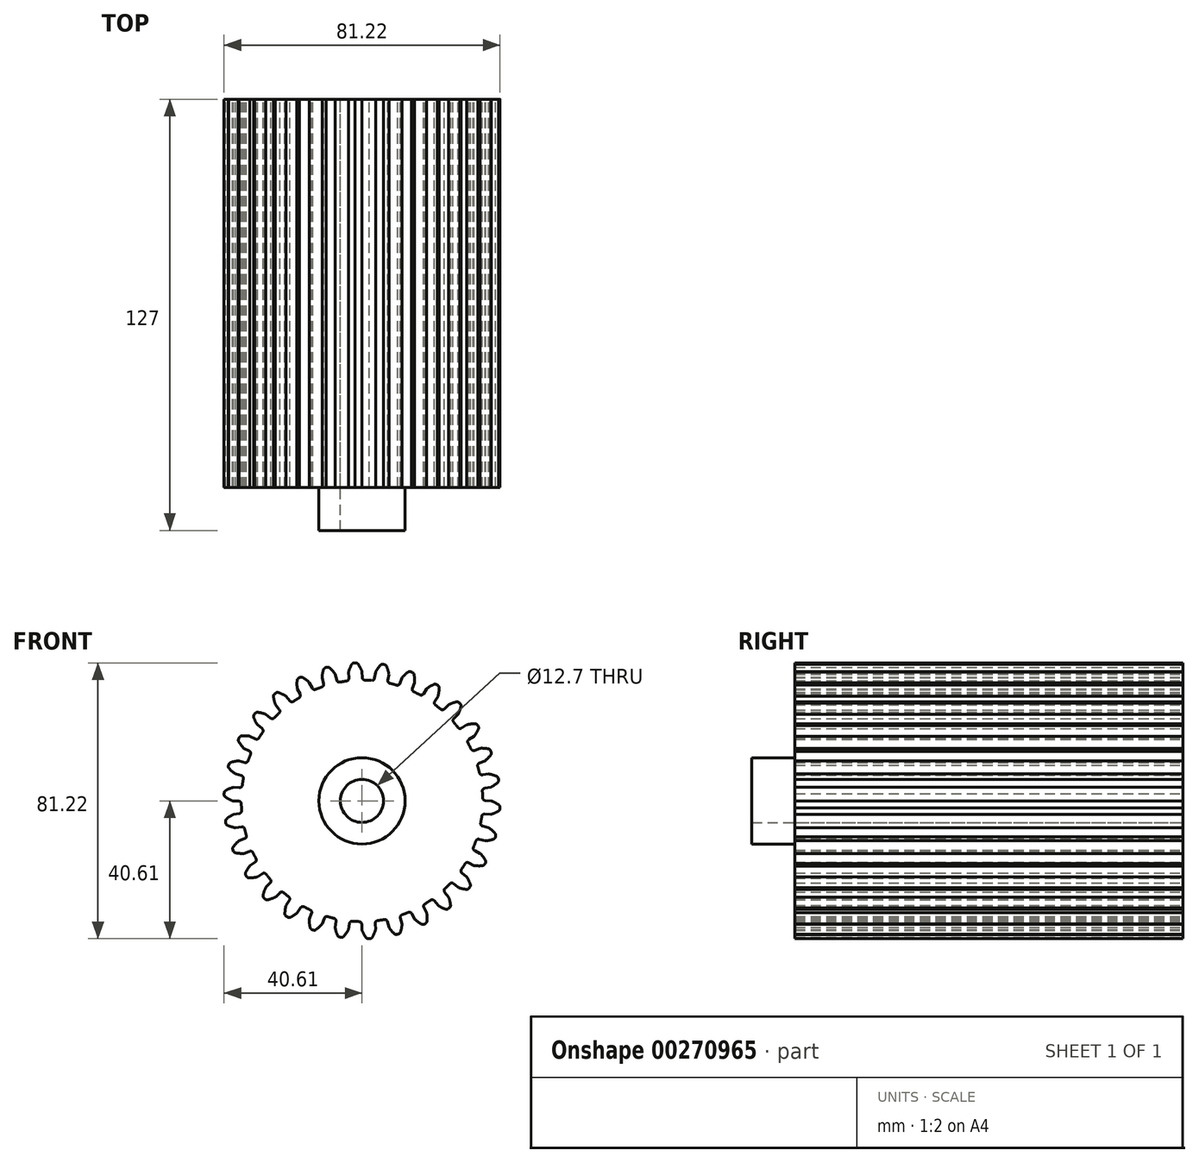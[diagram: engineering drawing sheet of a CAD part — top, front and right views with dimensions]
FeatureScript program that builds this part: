
annotation { "Feature Type Name" : "Feature", "Feature Type Description" : "" }
export const myFeature = defineFeature(function(context is Context, id is Id, definition is map)
    precondition{}
    {
        {
            var Q0;
            Q0=qCreatedBy(makeId("Front.planeOp"),FACE);
            var sketch = newSketch(context, id + "F0", { "sketchPlane" : qUnion([Q0])});
            skArc(sketch, "E0", {"start": v(-4.57, 35.26) * mm, "mid": v(-5.56, 35.12) * mm, "end": v(-6.55, 34.95) * mm});
            skArc(sketch, "E1.trimOffspring", {"start": v(0, 38.1) * mm, "mid": v(-0.52, 39.23) * mm, "end": v(-1.2, 40.3) * mm});
            skLineSegment(sketch, "E2", {"start": v(0, 38.1) * mm, "end": v(0.1, 36.3) * mm});
            skLineSegment(sketch, "E3", {"start": v(-1.83, 40.61) * mm, "end": v(-2.13, 40.61) * mm});
            skLineSegment(sketch, "E4.MirrorCS", {"start": v(-2.43, 40.58) * mm, "end": v(-2.13, 40.61) * mm});
            skArc(sketch, "E5.MirrorCS", {"start": v(-3.98, 37.9) * mm, "mid": v(-3.58, 39.07) * mm, "end": v(-3.03, 40.2) * mm});
            skLineSegment(sketch, "E6.MirrorCS", {"start": v(-3.98, 37.9) * mm, "end": v(-3.89, 36.09) * mm});
            skPoint(sketch, "E7.orphan", {"position": v(-3.43, 27.29) * mm});
            skPoint(sketch, "E8.orphan", {"position": v(0.56, 27.5) * mm});
            skPoint(sketch, "E9.visualSharp", {"position": v(-3.85, 35.35) * mm});
            skArc(sketch, "E9.filletArc", {"start": v(-4.57, 35.26) * mm, "mid": v(-4.07, 35.54) * mm, "end": v(-3.89, 36.09) * mm});
            skPoint(sketch, "E10.visualSharp", {"position": v(0.13, 35.56) * mm});
            skArc(sketch, "E10.filletArc", {"start": v(0.1, 36.3) * mm, "mid": v(0.33, 35.77) * mm, "end": v(0.86, 35.55) * mm});
            skPoint(sketch, "E11.visualSharp", {"position": v(-1.44, 40.61) * mm});
            skArc(sketch, "E11.filletArc", {"start": v(-1.2, 40.3) * mm, "mid": v(-1.47, 40.53) * mm, "end": v(-1.83, 40.61) * mm});
            skPoint(sketch, "E12.visualSharp", {"position": v(-2.81, 40.54) * mm});
            skArc(sketch, "E12.filletArc", {"start": v(-2.43, 40.58) * mm, "mid": v(-2.77, 40.46) * mm, "end": v(-3.03, 40.2) * mm});
            skCircle(sketch, "E13", {"center": v(0, 0) * mm, "radius": 6.35 * mm});
            skLineSegment(sketch, "E14.1.0", {"start": v(-7.92, 37.27) * mm, "end": v(-7.45, 35.52) * mm});
            skArc(sketch, "E14.1.1", {"start": v(-7.45, 35.52) * mm, "mid": v(-7.11, 35.06) * mm, "end": v(-6.55, 34.95) * mm});
            skArc(sketch, "E14.1.2", {"start": v(-7.92, 37.27) * mm, "mid": v(-8.67, 38.27) * mm, "end": v(-9.54, 39.16) * mm});
            skArc(sketch, "E14.1.3", {"start": v(-10.81, 39.2) * mm, "mid": v(-11.12, 39) * mm, "end": v(-11.32, 38.69) * mm});
            skLineSegment(sketch, "E14.1.4", {"start": v(-10.81, 39.2) * mm, "end": v(-10.53, 39.28) * mm});
            skLineSegment(sketch, "E14.1.5", {"start": v(-10.23, 39.35) * mm, "end": v(-10.53, 39.28) * mm});
            skArc(sketch, "E14.1.6", {"start": v(-9.54, 39.16) * mm, "mid": v(-9.87, 39.34) * mm, "end": v(-10.23, 39.35) * mm});
            skArc(sketch, "E14.1.7", {"start": v(-11.77, 36.24) * mm, "mid": v(-11.63, 37.48) * mm, "end": v(-11.32, 38.69) * mm});
            skLineSegment(sketch, "E14.1.8", {"start": v(-11.77, 36.24) * mm, "end": v(-11.3, 34.49) * mm});
            skArc(sketch, "E14.1.9", {"start": v(-11.8, 33.54) * mm, "mid": v(-11.37, 33.92) * mm, "end": v(-11.3, 34.49) * mm});
            skLineSegment(sketch, "E14.2.0", {"start": v(-15.5, 34.8) * mm, "end": v(-14.68, 33.2) * mm});
            skArc(sketch, "E14.2.1", {"start": v(-14.68, 33.2) * mm, "mid": v(-14.25, 32.81) * mm, "end": v(-13.67, 32.83) * mm});
            skArc(sketch, "E14.2.2", {"start": v(-15.5, 34.8) * mm, "mid": v(-16.44, 35.63) * mm, "end": v(-17.48, 36.32) * mm});
            skArc(sketch, "E14.2.3", {"start": v(-18.72, 36.09) * mm, "mid": v(-18.99, 35.84) * mm, "end": v(-19.11, 35.49) * mm});
            skLineSegment(sketch, "E14.2.4", {"start": v(-18.72, 36.09) * mm, "end": v(-18.46, 36.24) * mm});
            skLineSegment(sketch, "E14.2.5", {"start": v(-18.2, 36.36) * mm, "end": v(-18.46, 36.24) * mm});
            skArc(sketch, "E14.2.6", {"start": v(-17.48, 36.32) * mm, "mid": v(-17.83, 36.43) * mm, "end": v(-18.2, 36.36) * mm});
            skArc(sketch, "E14.2.7", {"start": v(-19.05, 33) * mm, "mid": v(-19.16, 34.24) * mm, "end": v(-19.11, 35.49) * mm});
            skLineSegment(sketch, "E14.2.8", {"start": v(-19.05, 33) * mm, "end": v(-18.23, 31.39) * mm});
            skArc(sketch, "E14.2.9", {"start": v(-18.52, 30.36) * mm, "mid": v(-18.17, 30.81) * mm, "end": v(-18.23, 31.39) * mm});
            skLineSegment(sketch, "E14.3.0", {"start": v(-22.4, 30.82) * mm, "end": v(-21.26, 29.42) * mm});
            skArc(sketch, "E14.3.1", {"start": v(-21.26, 29.42) * mm, "mid": v(-20.76, 29.14) * mm, "end": v(-20.2, 29.27) * mm});
            skArc(sketch, "E14.3.2", {"start": v(-22.4, 30.82) * mm, "mid": v(-23.49, 31.43) * mm, "end": v(-24.65, 31.9) * mm});
            skArc(sketch, "E14.3.3", {"start": v(-25.82, 31.4) * mm, "mid": v(-26.03, 31.1) * mm, "end": v(-26.07, 30.74) * mm});
            skLineSegment(sketch, "E14.3.4", {"start": v(-25.82, 31.4) * mm, "end": v(-25.6, 31.6) * mm});
            skLineSegment(sketch, "E14.3.5", {"start": v(-25.35, 31.78) * mm, "end": v(-25.6, 31.6) * mm});
            skArc(sketch, "E14.3.6", {"start": v(-24.65, 31.9) * mm, "mid": v(-25.01, 31.92) * mm, "end": v(-25.35, 31.78) * mm});
            skArc(sketch, "E14.3.7", {"start": v(-25.5, 28.31) * mm, "mid": v(-25.86, 29.5) * mm, "end": v(-26.07, 30.74) * mm});
            skLineSegment(sketch, "E14.3.8", {"start": v(-25.5, 28.31) * mm, "end": v(-24.36, 26.9) * mm});
            skArc(sketch, "E14.3.9", {"start": v(-24.43, 25.84) * mm, "mid": v(-24.18, 26.36) * mm, "end": v(-24.36, 26.9) * mm});
            skLineSegment(sketch, "E14.4.0", {"start": v(-28.31, 25.5) * mm, "end": v(-26.9, 24.36) * mm});
            skArc(sketch, "E14.4.1", {"start": v(-26.9, 24.36) * mm, "mid": v(-26.36, 24.18) * mm, "end": v(-25.84, 24.43) * mm});
            skArc(sketch, "E14.4.2", {"start": v(-28.31, 25.5) * mm, "mid": v(-29.5, 25.86) * mm, "end": v(-30.74, 26.07) * mm});
            skArc(sketch, "E14.4.3", {"start": v(-31.78, 25.35) * mm, "mid": v(-31.92, 25.01) * mm, "end": v(-31.9, 24.65) * mm});
            skLineSegment(sketch, "E14.4.4", {"start": v(-31.78, 25.35) * mm, "end": v(-31.6, 25.6) * mm});
            skLineSegment(sketch, "E14.4.5", {"start": v(-31.4, 25.82) * mm, "end": v(-31.6, 25.6) * mm});
            skArc(sketch, "E14.4.6", {"start": v(-30.74, 26.07) * mm, "mid": v(-31.1, 26.03) * mm, "end": v(-31.4, 25.82) * mm});
            skArc(sketch, "E14.4.7", {"start": v(-30.82, 22.4) * mm, "mid": v(-31.43, 23.49) * mm, "end": v(-31.9, 24.65) * mm});
            skLineSegment(sketch, "E14.4.8", {"start": v(-30.82, 22.4) * mm, "end": v(-29.42, 21.26) * mm});
            skArc(sketch, "E14.4.9", {"start": v(-29.27, 20.2) * mm, "mid": v(-29.14, 20.76) * mm, "end": v(-29.42, 21.26) * mm});
            skLineSegment(sketch, "E14.5.0", {"start": v(-33, 19.05) * mm, "end": v(-31.39, 18.23) * mm});
            skArc(sketch, "E14.5.1", {"start": v(-31.39, 18.23) * mm, "mid": v(-30.81, 18.17) * mm, "end": v(-30.36, 18.52) * mm});
            skArc(sketch, "E14.5.2", {"start": v(-33, 19.05) * mm, "mid": v(-34.24, 19.16) * mm, "end": v(-35.49, 19.11) * mm});
            skArc(sketch, "E14.5.3", {"start": v(-36.36, 18.2) * mm, "mid": v(-36.43, 17.83) * mm, "end": v(-36.32, 17.48) * mm});
            skLineSegment(sketch, "E14.5.4", {"start": v(-36.36, 18.2) * mm, "end": v(-36.24, 18.46) * mm});
            skLineSegment(sketch, "E14.5.5", {"start": v(-36.09, 18.72) * mm, "end": v(-36.24, 18.46) * mm});
            skArc(sketch, "E14.5.6", {"start": v(-35.49, 19.11) * mm, "mid": v(-35.84, 18.99) * mm, "end": v(-36.09, 18.72) * mm});
            skArc(sketch, "E14.5.7", {"start": v(-34.8, 15.5) * mm, "mid": v(-35.63, 16.44) * mm, "end": v(-36.32, 17.48) * mm});
            skLineSegment(sketch, "E14.5.8", {"start": v(-34.8, 15.5) * mm, "end": v(-33.2, 14.68) * mm});
            skArc(sketch, "E14.5.9", {"start": v(-32.83, 13.67) * mm, "mid": v(-32.81, 14.25) * mm, "end": v(-33.2, 14.68) * mm});
            skLineSegment(sketch, "E14.6.0", {"start": v(-36.24, 11.77) * mm, "end": v(-34.49, 11.3) * mm});
            skArc(sketch, "E14.6.1", {"start": v(-34.49, 11.3) * mm, "mid": v(-33.92, 11.37) * mm, "end": v(-33.54, 11.8) * mm});
            skArc(sketch, "E14.6.2", {"start": v(-36.24, 11.77) * mm, "mid": v(-37.48, 11.63) * mm, "end": v(-38.69, 11.32) * mm});
            skArc(sketch, "E14.6.3", {"start": v(-39.35, 10.23) * mm, "mid": v(-39.34, 9.87) * mm, "end": v(-39.16, 9.54) * mm});
            skLineSegment(sketch, "E14.6.4", {"start": v(-39.35, 10.23) * mm, "end": v(-39.28, 10.53) * mm});
            skLineSegment(sketch, "E14.6.5", {"start": v(-39.2, 10.81) * mm, "end": v(-39.28, 10.53) * mm});
            skArc(sketch, "E14.6.6", {"start": v(-38.69, 11.32) * mm, "mid": v(-39, 11.12) * mm, "end": v(-39.2, 10.81) * mm});
            skArc(sketch, "E14.6.7", {"start": v(-37.27, 7.92) * mm, "mid": v(-38.27, 8.67) * mm, "end": v(-39.16, 9.54) * mm});
            skLineSegment(sketch, "E14.6.8", {"start": v(-37.27, 7.92) * mm, "end": v(-35.52, 7.45) * mm});
            skArc(sketch, "E14.6.9", {"start": v(-34.95, 6.55) * mm, "mid": v(-35.06, 7.11) * mm, "end": v(-35.52, 7.45) * mm});
            skLineSegment(sketch, "E14.7.0", {"start": v(-37.9, 3.98) * mm, "end": v(-36.09, 3.89) * mm});
            skArc(sketch, "E14.7.1", {"start": v(-36.09, 3.89) * mm, "mid": v(-35.54, 4.07) * mm, "end": v(-35.26, 4.57) * mm});
            skArc(sketch, "E14.7.2", {"start": v(-37.9, 3.98) * mm, "mid": v(-39.07, 3.58) * mm, "end": v(-40.2, 3.03) * mm});
            skArc(sketch, "E14.7.3", {"start": v(-40.61, 1.83) * mm, "mid": v(-40.53, 1.47) * mm, "end": v(-40.3, 1.2) * mm});
            skLineSegment(sketch, "E14.7.4", {"start": v(-40.61, 1.83) * mm, "end": v(-40.61, 2.13) * mm});
            skLineSegment(sketch, "E14.7.5", {"start": v(-40.58, 2.43) * mm, "end": v(-40.61, 2.13) * mm});
            skArc(sketch, "E14.7.6", {"start": v(-40.2, 3.03) * mm, "mid": v(-40.46, 2.77) * mm, "end": v(-40.58, 2.43) * mm});
            skArc(sketch, "E14.7.7", {"start": v(-38.1, 0) * mm, "mid": v(-39.23, 0.52) * mm, "end": v(-40.3, 1.2) * mm});
            skLineSegment(sketch, "E14.7.8", {"start": v(-38.1, 0) * mm, "end": v(-36.3, -0.1) * mm});
            skArc(sketch, "E14.7.9", {"start": v(-35.55, -0.86) * mm, "mid": v(-35.77, -0.33) * mm, "end": v(-36.3, -0.1) * mm});
            skLineSegment(sketch, "E14.8.0", {"start": v(-37.9, -3.98) * mm, "end": v(-36.1, -3.7) * mm});
            skArc(sketch, "E14.8.1", {"start": v(-36.1, -3.7) * mm, "mid": v(-35.61, -3.4) * mm, "end": v(-35.44, -2.86) * mm});
            skArc(sketch, "E14.8.2", {"start": v(-37.9, -3.98) * mm, "mid": v(-38.96, -4.62) * mm, "end": v(-39.95, -5.4) * mm});
            skArc(sketch, "E14.8.3", {"start": v(-40.1, -6.66) * mm, "mid": v(-39.95, -6.99) * mm, "end": v(-39.66, -7.21) * mm});
            skLineSegment(sketch, "E14.8.4", {"start": v(-40.1, -6.66) * mm, "end": v(-40.17, -6.36) * mm});
            skLineSegment(sketch, "E14.8.5", {"start": v(-40.2, -6.06) * mm, "end": v(-40.17, -6.36) * mm});
            skArc(sketch, "E14.8.6", {"start": v(-39.95, -5.4) * mm, "mid": v(-40.15, -5.7) * mm, "end": v(-40.2, -6.06) * mm});
            skArc(sketch, "E14.8.7", {"start": v(-37.27, -7.92) * mm, "mid": v(-38.49, -7.64) * mm, "end": v(-39.66, -7.21) * mm});
            skLineSegment(sketch, "E14.8.8", {"start": v(-37.27, -7.92) * mm, "end": v(-35.48, -7.64) * mm});
            skArc(sketch, "E14.8.9", {"start": v(-34.6, -8.23) * mm, "mid": v(-34.92, -7.76) * mm, "end": v(-35.48, -7.64) * mm});
            skLineSegment(sketch, "E14.9.0", {"start": v(-36.24, -11.77) * mm, "end": v(-34.55, -11.13) * mm});
            skArc(sketch, "E14.9.1", {"start": v(-34.55, -11.13) * mm, "mid": v(-34.12, -10.74) * mm, "end": v(-34.08, -10.17) * mm});
            skArc(sketch, "E14.9.2", {"start": v(-36.24, -11.77) * mm, "mid": v(-37.15, -12.62) * mm, "end": v(-37.95, -13.58) * mm});
            skArc(sketch, "E14.9.3", {"start": v(-37.85, -14.85) * mm, "mid": v(-37.62, -15.14) * mm, "end": v(-37.3, -15.3) * mm});
            skLineSegment(sketch, "E14.9.4", {"start": v(-37.85, -14.85) * mm, "end": v(-37.97, -14.57) * mm});
            skLineSegment(sketch, "E14.9.5", {"start": v(-38.06, -14.29) * mm, "end": v(-37.97, -14.57) * mm});
            skArc(sketch, "E14.9.6", {"start": v(-37.95, -13.58) * mm, "mid": v(-38.1, -13.92) * mm, "end": v(-38.06, -14.29) * mm});
            skArc(sketch, "E14.9.7", {"start": v(-34.8, -15.5) * mm, "mid": v(-36.06, -15.48) * mm, "end": v(-37.3, -15.3) * mm});
            skLineSegment(sketch, "E14.9.8", {"start": v(-34.8, -15.5) * mm, "end": v(-33.12, -14.85) * mm});
            skArc(sketch, "E14.9.9", {"start": v(-32.13, -15.25) * mm, "mid": v(-32.54, -14.85) * mm, "end": v(-33.12, -14.85) * mm});
            skLineSegment(sketch, "E14.10.0", {"start": v(-33, -19.05) * mm, "end": v(-31.48, -18.07) * mm});
            skArc(sketch, "E14.10.1", {"start": v(-31.48, -18.07) * mm, "mid": v(-31.15, -17.6) * mm, "end": v(-31.22, -17.03) * mm});
            skArc(sketch, "E14.10.2", {"start": v(-33, -19.05) * mm, "mid": v(-33.72, -20.07) * mm, "end": v(-34.3, -21.18) * mm});
            skArc(sketch, "E14.10.3", {"start": v(-33.93, -22.4) * mm, "mid": v(-33.65, -22.63) * mm, "end": v(-33.3, -22.72) * mm});
            skLineSegment(sketch, "E14.10.4", {"start": v(-33.93, -22.4) * mm, "end": v(-34.1, -22.15) * mm});
            skLineSegment(sketch, "E14.10.5", {"start": v(-34.26, -21.9) * mm, "end": v(-34.1, -22.15) * mm});
            skArc(sketch, "E14.10.6", {"start": v(-34.3, -21.18) * mm, "mid": v(-34.36, -21.54) * mm, "end": v(-34.26, -21.9) * mm});
            skArc(sketch, "E14.10.7", {"start": v(-30.82, -22.4) * mm, "mid": v(-32.05, -22.64) * mm, "end": v(-33.3, -22.72) * mm});
            skLineSegment(sketch, "E14.10.8", {"start": v(-30.82, -22.4) * mm, "end": v(-29.3, -21.41) * mm});
            skArc(sketch, "E14.10.9", {"start": v(-28.25, -21.6) * mm, "mid": v(-28.75, -21.3) * mm, "end": v(-29.3, -21.41) * mm});
            skLineSegment(sketch, "E14.11.0", {"start": v(-28.31, -25.5) * mm, "end": v(-27.04, -24.22) * mm});
            skArc(sketch, "E14.11.1", {"start": v(-27.04, -24.22) * mm, "mid": v(-26.8, -23.69) * mm, "end": v(-27, -23.15) * mm});
            skArc(sketch, "E14.11.2", {"start": v(-28.31, -25.5) * mm, "mid": v(-28.8, -26.64) * mm, "end": v(-29.14, -27.85) * mm});
            skArc(sketch, "E14.11.3", {"start": v(-28.54, -28.96) * mm, "mid": v(-28.21, -29.13) * mm, "end": v(-27.85, -29.14) * mm});
            skLineSegment(sketch, "E14.11.4", {"start": v(-28.54, -28.96) * mm, "end": v(-28.76, -28.76) * mm});
            skLineSegment(sketch, "E14.11.5", {"start": v(-28.96, -28.54) * mm, "end": v(-28.76, -28.76) * mm});
            skArc(sketch, "E14.11.6", {"start": v(-29.14, -27.85) * mm, "mid": v(-29.13, -28.21) * mm, "end": v(-28.96, -28.54) * mm});
            skArc(sketch, "E14.11.7", {"start": v(-25.5, -28.31) * mm, "mid": v(-26.64, -28.8) * mm, "end": v(-27.85, -29.14) * mm});
            skLineSegment(sketch, "E14.11.8", {"start": v(-25.5, -28.31) * mm, "end": v(-24.22, -27.04) * mm});
            skArc(sketch, "E14.11.9", {"start": v(-23.15, -27) * mm, "mid": v(-23.69, -26.8) * mm, "end": v(-24.22, -27.04) * mm});
            skLineSegment(sketch, "E14.12.0", {"start": v(-22.4, -30.82) * mm, "end": v(-21.41, -29.3) * mm});
            skArc(sketch, "E14.12.1", {"start": v(-21.41, -29.3) * mm, "mid": v(-21.3, -28.75) * mm, "end": v(-21.6, -28.25) * mm});
            skArc(sketch, "E14.12.2", {"start": v(-22.4, -30.82) * mm, "mid": v(-22.64, -32.05) * mm, "end": v(-22.72, -33.3) * mm});
            skArc(sketch, "E14.12.3", {"start": v(-21.9, -34.26) * mm, "mid": v(-21.54, -34.36) * mm, "end": v(-21.18, -34.3) * mm});
            skLineSegment(sketch, "E14.12.4", {"start": v(-21.9, -34.26) * mm, "end": v(-22.15, -34.1) * mm});
            skLineSegment(sketch, "E14.12.5", {"start": v(-22.4, -33.93) * mm, "end": v(-22.15, -34.1) * mm});
            skArc(sketch, "E14.12.6", {"start": v(-22.72, -33.3) * mm, "mid": v(-22.63, -33.65) * mm, "end": v(-22.4, -33.93) * mm});
            skArc(sketch, "E14.12.7", {"start": v(-19.05, -33) * mm, "mid": v(-20.07, -33.72) * mm, "end": v(-21.18, -34.3) * mm});
            skLineSegment(sketch, "E14.12.8", {"start": v(-19.05, -33) * mm, "end": v(-18.07, -31.48) * mm});
            skArc(sketch, "E14.12.9", {"start": v(-17.03, -31.22) * mm, "mid": v(-17.6, -31.15) * mm, "end": v(-18.07, -31.48) * mm});
            skLineSegment(sketch, "E14.13.0", {"start": v(-15.5, -34.8) * mm, "end": v(-14.85, -33.12) * mm});
            skArc(sketch, "E14.13.1", {"start": v(-14.85, -33.12) * mm, "mid": v(-14.85, -32.54) * mm, "end": v(-15.25, -32.13) * mm});
            skArc(sketch, "E14.13.2", {"start": v(-15.5, -34.8) * mm, "mid": v(-15.48, -36.06) * mm, "end": v(-15.3, -37.3) * mm});
            skArc(sketch, "E14.13.3", {"start": v(-14.29, -38.06) * mm, "mid": v(-13.92, -38.1) * mm, "end": v(-13.58, -37.95) * mm});
            skLineSegment(sketch, "E14.13.4", {"start": v(-14.29, -38.06) * mm, "end": v(-14.57, -37.97) * mm});
            skLineSegment(sketch, "E14.13.5", {"start": v(-14.85, -37.85) * mm, "end": v(-14.57, -37.97) * mm});
            skArc(sketch, "E14.13.6", {"start": v(-15.3, -37.3) * mm, "mid": v(-15.14, -37.62) * mm, "end": v(-14.85, -37.85) * mm});
            skArc(sketch, "E14.13.7", {"start": v(-11.77, -36.24) * mm, "mid": v(-12.62, -37.15) * mm, "end": v(-13.58, -37.95) * mm});
            skLineSegment(sketch, "E14.13.8", {"start": v(-11.77, -36.24) * mm, "end": v(-11.13, -34.55) * mm});
            skArc(sketch, "E14.13.9", {"start": v(-10.17, -34.08) * mm, "mid": v(-10.74, -34.12) * mm, "end": v(-11.13, -34.55) * mm});
            skLineSegment(sketch, "E14.14.0", {"start": v(-7.92, -37.27) * mm, "end": v(-7.64, -35.48) * mm});
            skArc(sketch, "E14.14.1", {"start": v(-7.64, -35.48) * mm, "mid": v(-7.76, -34.92) * mm, "end": v(-8.23, -34.6) * mm});
            skArc(sketch, "E14.14.2", {"start": v(-7.92, -37.27) * mm, "mid": v(-7.64, -38.49) * mm, "end": v(-7.21, -39.66) * mm});
            skArc(sketch, "E14.14.3", {"start": v(-6.06, -40.2) * mm, "mid": v(-5.7, -40.15) * mm, "end": v(-5.4, -39.95) * mm});
            skLineSegment(sketch, "E14.14.4", {"start": v(-6.06, -40.2) * mm, "end": v(-6.36, -40.17) * mm});
            skLineSegment(sketch, "E14.14.5", {"start": v(-6.66, -40.1) * mm, "end": v(-6.36, -40.17) * mm});
            skArc(sketch, "E14.14.6", {"start": v(-7.21, -39.66) * mm, "mid": v(-6.99, -39.95) * mm, "end": v(-6.66, -40.1) * mm});
            skArc(sketch, "E14.14.7", {"start": v(-3.98, -37.9) * mm, "mid": v(-4.62, -38.96) * mm, "end": v(-5.4, -39.95) * mm});
            skLineSegment(sketch, "E14.14.8", {"start": v(-3.98, -37.9) * mm, "end": v(-3.7, -36.1) * mm});
            skArc(sketch, "E14.14.9", {"start": v(-2.86, -35.44) * mm, "mid": v(-3.4, -35.61) * mm, "end": v(-3.7, -36.1) * mm});
            skLineSegment(sketch, "E14.15.0", {"start": v(0, -38.1) * mm, "end": v(-0.1, -36.3) * mm});
            skArc(sketch, "E14.15.1", {"start": v(-0.1, -36.3) * mm, "mid": v(-0.33, -35.77) * mm, "end": v(-0.86, -35.55) * mm});
            skArc(sketch, "E14.15.2", {"start": v(0, -38.1) * mm, "mid": v(0.52, -39.23) * mm, "end": v(1.2, -40.3) * mm});
            skArc(sketch, "E14.15.3", {"start": v(2.43, -40.58) * mm, "mid": v(2.77, -40.46) * mm, "end": v(3.03, -40.2) * mm});
            skLineSegment(sketch, "E14.15.4", {"start": v(2.43, -40.58) * mm, "end": v(2.13, -40.61) * mm});
            skLineSegment(sketch, "E14.15.5", {"start": v(1.83, -40.61) * mm, "end": v(2.13, -40.61) * mm});
            skArc(sketch, "E14.15.6", {"start": v(1.2, -40.3) * mm, "mid": v(1.47, -40.53) * mm, "end": v(1.83, -40.61) * mm});
            skArc(sketch, "E14.15.7", {"start": v(3.98, -37.9) * mm, "mid": v(3.58, -39.07) * mm, "end": v(3.03, -40.2) * mm});
            skLineSegment(sketch, "E14.15.8", {"start": v(3.98, -37.9) * mm, "end": v(3.89, -36.09) * mm});
            skArc(sketch, "E14.15.9", {"start": v(4.57, -35.26) * mm, "mid": v(4.07, -35.54) * mm, "end": v(3.89, -36.09) * mm});
            skLineSegment(sketch, "E14.16.0", {"start": v(7.92, -37.27) * mm, "end": v(7.45, -35.52) * mm});
            skArc(sketch, "E14.16.1", {"start": v(7.45, -35.52) * mm, "mid": v(7.11, -35.06) * mm, "end": v(6.55, -34.95) * mm});
            skArc(sketch, "E14.16.2", {"start": v(7.92, -37.27) * mm, "mid": v(8.67, -38.27) * mm, "end": v(9.54, -39.16) * mm});
            skArc(sketch, "E14.16.3", {"start": v(10.81, -39.2) * mm, "mid": v(11.12, -39) * mm, "end": v(11.32, -38.69) * mm});
            skLineSegment(sketch, "E14.16.4", {"start": v(10.81, -39.2) * mm, "end": v(10.53, -39.28) * mm});
            skLineSegment(sketch, "E14.16.5", {"start": v(10.23, -39.35) * mm, "end": v(10.53, -39.28) * mm});
            skArc(sketch, "E14.16.6", {"start": v(9.54, -39.16) * mm, "mid": v(9.87, -39.34) * mm, "end": v(10.23, -39.35) * mm});
            skArc(sketch, "E14.16.7", {"start": v(11.77, -36.24) * mm, "mid": v(11.63, -37.48) * mm, "end": v(11.32, -38.69) * mm});
            skLineSegment(sketch, "E14.16.8", {"start": v(11.77, -36.24) * mm, "end": v(11.3, -34.49) * mm});
            skArc(sketch, "E14.16.9", {"start": v(11.8, -33.54) * mm, "mid": v(11.37, -33.92) * mm, "end": v(11.3, -34.49) * mm});
            skLineSegment(sketch, "E14.17.0", {"start": v(15.5, -34.8) * mm, "end": v(14.68, -33.2) * mm});
            skArc(sketch, "E14.17.1", {"start": v(14.68, -33.2) * mm, "mid": v(14.25, -32.81) * mm, "end": v(13.67, -32.83) * mm});
            skArc(sketch, "E14.17.2", {"start": v(15.5, -34.8) * mm, "mid": v(16.44, -35.63) * mm, "end": v(17.48, -36.32) * mm});
            skArc(sketch, "E14.17.3", {"start": v(18.72, -36.09) * mm, "mid": v(18.99, -35.84) * mm, "end": v(19.11, -35.49) * mm});
            skLineSegment(sketch, "E14.17.4", {"start": v(18.72, -36.09) * mm, "end": v(18.46, -36.24) * mm});
            skLineSegment(sketch, "E14.17.5", {"start": v(18.2, -36.36) * mm, "end": v(18.46, -36.24) * mm});
            skArc(sketch, "E14.17.6", {"start": v(17.48, -36.32) * mm, "mid": v(17.83, -36.43) * mm, "end": v(18.2, -36.36) * mm});
            skArc(sketch, "E14.17.7", {"start": v(19.05, -33) * mm, "mid": v(19.16, -34.24) * mm, "end": v(19.11, -35.49) * mm});
            skLineSegment(sketch, "E14.17.8", {"start": v(19.05, -33) * mm, "end": v(18.23, -31.39) * mm});
            skArc(sketch, "E14.17.9", {"start": v(18.52, -30.36) * mm, "mid": v(18.17, -30.81) * mm, "end": v(18.23, -31.39) * mm});
            skLineSegment(sketch, "E14.18.0", {"start": v(22.4, -30.82) * mm, "end": v(21.26, -29.42) * mm});
            skArc(sketch, "E14.18.1", {"start": v(21.26, -29.42) * mm, "mid": v(20.76, -29.14) * mm, "end": v(20.2, -29.27) * mm});
            skArc(sketch, "E14.18.2", {"start": v(22.4, -30.82) * mm, "mid": v(23.49, -31.43) * mm, "end": v(24.65, -31.9) * mm});
            skArc(sketch, "E14.18.3", {"start": v(25.82, -31.4) * mm, "mid": v(26.03, -31.1) * mm, "end": v(26.07, -30.74) * mm});
            skLineSegment(sketch, "E14.18.4", {"start": v(25.82, -31.4) * mm, "end": v(25.6, -31.6) * mm});
            skLineSegment(sketch, "E14.18.5", {"start": v(25.35, -31.78) * mm, "end": v(25.6, -31.6) * mm});
            skArc(sketch, "E14.18.6", {"start": v(24.65, -31.9) * mm, "mid": v(25.01, -31.92) * mm, "end": v(25.35, -31.78) * mm});
            skArc(sketch, "E14.18.7", {"start": v(25.5, -28.31) * mm, "mid": v(25.86, -29.5) * mm, "end": v(26.07, -30.74) * mm});
            skLineSegment(sketch, "E14.18.8", {"start": v(25.5, -28.31) * mm, "end": v(24.36, -26.9) * mm});
            skArc(sketch, "E14.18.9", {"start": v(24.43, -25.84) * mm, "mid": v(24.18, -26.36) * mm, "end": v(24.36, -26.9) * mm});
            skLineSegment(sketch, "E14.19.0", {"start": v(28.31, -25.5) * mm, "end": v(26.9, -24.36) * mm});
            skArc(sketch, "E14.19.1", {"start": v(26.9, -24.36) * mm, "mid": v(26.36, -24.18) * mm, "end": v(25.84, -24.43) * mm});
            skArc(sketch, "E14.19.2", {"start": v(28.31, -25.5) * mm, "mid": v(29.5, -25.86) * mm, "end": v(30.74, -26.07) * mm});
            skArc(sketch, "E14.19.3", {"start": v(31.78, -25.35) * mm, "mid": v(31.92, -25.01) * mm, "end": v(31.9, -24.65) * mm});
            skLineSegment(sketch, "E14.19.4", {"start": v(31.78, -25.35) * mm, "end": v(31.6, -25.6) * mm});
            skLineSegment(sketch, "E14.19.5", {"start": v(31.4, -25.82) * mm, "end": v(31.6, -25.6) * mm});
            skArc(sketch, "E14.19.6", {"start": v(30.74, -26.07) * mm, "mid": v(31.1, -26.03) * mm, "end": v(31.4, -25.82) * mm});
            skArc(sketch, "E14.19.7", {"start": v(30.82, -22.4) * mm, "mid": v(31.43, -23.49) * mm, "end": v(31.9, -24.65) * mm});
            skLineSegment(sketch, "E14.19.8", {"start": v(30.82, -22.4) * mm, "end": v(29.42, -21.26) * mm});
            skArc(sketch, "E14.19.9", {"start": v(29.27, -20.2) * mm, "mid": v(29.14, -20.76) * mm, "end": v(29.42, -21.26) * mm});
            skLineSegment(sketch, "E14.20.0", {"start": v(33, -19.05) * mm, "end": v(31.39, -18.23) * mm});
            skArc(sketch, "E14.20.1", {"start": v(31.39, -18.23) * mm, "mid": v(30.81, -18.17) * mm, "end": v(30.36, -18.52) * mm});
            skArc(sketch, "E14.20.2", {"start": v(33, -19.05) * mm, "mid": v(34.24, -19.16) * mm, "end": v(35.49, -19.11) * mm});
            skArc(sketch, "E14.20.3", {"start": v(36.36, -18.2) * mm, "mid": v(36.43, -17.83) * mm, "end": v(36.32, -17.48) * mm});
            skLineSegment(sketch, "E14.20.4", {"start": v(36.36, -18.2) * mm, "end": v(36.24, -18.46) * mm});
            skLineSegment(sketch, "E14.20.5", {"start": v(36.09, -18.72) * mm, "end": v(36.24, -18.46) * mm});
            skArc(sketch, "E14.20.6", {"start": v(35.49, -19.11) * mm, "mid": v(35.84, -18.99) * mm, "end": v(36.09, -18.72) * mm});
            skArc(sketch, "E14.20.7", {"start": v(34.8, -15.5) * mm, "mid": v(35.63, -16.44) * mm, "end": v(36.32, -17.48) * mm});
            skLineSegment(sketch, "E14.20.8", {"start": v(34.8, -15.5) * mm, "end": v(33.2, -14.68) * mm});
            skArc(sketch, "E14.20.9", {"start": v(32.83, -13.67) * mm, "mid": v(32.81, -14.25) * mm, "end": v(33.2, -14.68) * mm});
            skLineSegment(sketch, "E14.21.0", {"start": v(36.24, -11.77) * mm, "end": v(34.49, -11.3) * mm});
            skArc(sketch, "E14.21.1", {"start": v(34.49, -11.3) * mm, "mid": v(33.92, -11.37) * mm, "end": v(33.54, -11.8) * mm});
            skArc(sketch, "E14.21.2", {"start": v(36.24, -11.77) * mm, "mid": v(37.48, -11.63) * mm, "end": v(38.69, -11.32) * mm});
            skArc(sketch, "E14.21.3", {"start": v(39.35, -10.23) * mm, "mid": v(39.34, -9.87) * mm, "end": v(39.16, -9.54) * mm});
            skLineSegment(sketch, "E14.21.4", {"start": v(39.35, -10.23) * mm, "end": v(39.28, -10.53) * mm});
            skLineSegment(sketch, "E14.21.5", {"start": v(39.2, -10.81) * mm, "end": v(39.28, -10.53) * mm});
            skArc(sketch, "E14.21.6", {"start": v(38.69, -11.32) * mm, "mid": v(39, -11.12) * mm, "end": v(39.2, -10.81) * mm});
            skArc(sketch, "E14.21.7", {"start": v(37.27, -7.92) * mm, "mid": v(38.27, -8.67) * mm, "end": v(39.16, -9.54) * mm});
            skLineSegment(sketch, "E14.21.8", {"start": v(37.27, -7.92) * mm, "end": v(35.52, -7.45) * mm});
            skArc(sketch, "E14.21.9", {"start": v(34.95, -6.55) * mm, "mid": v(35.06, -7.11) * mm, "end": v(35.52, -7.45) * mm});
            skLineSegment(sketch, "E14.22.0", {"start": v(37.9, -3.98) * mm, "end": v(36.09, -3.89) * mm});
            skArc(sketch, "E14.22.1", {"start": v(36.09, -3.89) * mm, "mid": v(35.54, -4.07) * mm, "end": v(35.26, -4.57) * mm});
            skArc(sketch, "E14.22.2", {"start": v(37.9, -3.98) * mm, "mid": v(39.07, -3.58) * mm, "end": v(40.2, -3.03) * mm});
            skArc(sketch, "E14.22.3", {"start": v(40.61, -1.83) * mm, "mid": v(40.53, -1.47) * mm, "end": v(40.3, -1.2) * mm});
            skLineSegment(sketch, "E14.22.4", {"start": v(40.61, -1.83) * mm, "end": v(40.61, -2.13) * mm});
            skLineSegment(sketch, "E14.22.5", {"start": v(40.58, -2.43) * mm, "end": v(40.61, -2.13) * mm});
            skArc(sketch, "E14.22.6", {"start": v(40.2, -3.03) * mm, "mid": v(40.46, -2.77) * mm, "end": v(40.58, -2.43) * mm});
            skArc(sketch, "E14.22.7", {"start": v(38.1, 0) * mm, "mid": v(39.23, -0.52) * mm, "end": v(40.3, -1.2) * mm});
            skLineSegment(sketch, "E14.22.8", {"start": v(38.1, 0) * mm, "end": v(36.3, 0.1) * mm});
            skArc(sketch, "E14.22.9", {"start": v(35.55, 0.86) * mm, "mid": v(35.77, 0.33) * mm, "end": v(36.3, 0.1) * mm});
            skLineSegment(sketch, "E14.23.0", {"start": v(37.9, 3.98) * mm, "end": v(36.1, 3.7) * mm});
            skArc(sketch, "E14.23.1", {"start": v(36.1, 3.7) * mm, "mid": v(35.61, 3.4) * mm, "end": v(35.44, 2.86) * mm});
            skArc(sketch, "E14.23.2", {"start": v(37.9, 3.98) * mm, "mid": v(38.96, 4.62) * mm, "end": v(39.95, 5.4) * mm});
            skArc(sketch, "E14.23.3", {"start": v(40.1, 6.66) * mm, "mid": v(39.95, 6.99) * mm, "end": v(39.66, 7.21) * mm});
            skLineSegment(sketch, "E14.23.4", {"start": v(40.1, 6.66) * mm, "end": v(40.17, 6.36) * mm});
            skLineSegment(sketch, "E14.23.5", {"start": v(40.2, 6.06) * mm, "end": v(40.17, 6.36) * mm});
            skArc(sketch, "E14.23.6", {"start": v(39.95, 5.4) * mm, "mid": v(40.15, 5.7) * mm, "end": v(40.2, 6.06) * mm});
            skArc(sketch, "E14.23.7", {"start": v(37.27, 7.92) * mm, "mid": v(38.49, 7.64) * mm, "end": v(39.66, 7.21) * mm});
            skLineSegment(sketch, "E14.23.8", {"start": v(37.27, 7.92) * mm, "end": v(35.48, 7.64) * mm});
            skArc(sketch, "E14.23.9", {"start": v(34.6, 8.23) * mm, "mid": v(34.92, 7.76) * mm, "end": v(35.48, 7.64) * mm});
            skLineSegment(sketch, "E14.24.0", {"start": v(36.24, 11.77) * mm, "end": v(34.55, 11.13) * mm});
            skArc(sketch, "E14.24.1", {"start": v(34.55, 11.13) * mm, "mid": v(34.12, 10.74) * mm, "end": v(34.08, 10.17) * mm});
            skArc(sketch, "E14.24.2", {"start": v(36.24, 11.77) * mm, "mid": v(37.15, 12.62) * mm, "end": v(37.95, 13.58) * mm});
            skArc(sketch, "E14.24.3", {"start": v(37.85, 14.85) * mm, "mid": v(37.62, 15.14) * mm, "end": v(37.3, 15.3) * mm});
            skLineSegment(sketch, "E14.24.4", {"start": v(37.85, 14.85) * mm, "end": v(37.97, 14.57) * mm});
            skLineSegment(sketch, "E14.24.5", {"start": v(38.06, 14.29) * mm, "end": v(37.97, 14.57) * mm});
            skArc(sketch, "E14.24.6", {"start": v(37.95, 13.58) * mm, "mid": v(38.1, 13.92) * mm, "end": v(38.06, 14.29) * mm});
            skArc(sketch, "E14.24.7", {"start": v(34.8, 15.5) * mm, "mid": v(36.06, 15.48) * mm, "end": v(37.3, 15.3) * mm});
            skLineSegment(sketch, "E14.24.8", {"start": v(34.8, 15.5) * mm, "end": v(33.12, 14.85) * mm});
            skArc(sketch, "E14.24.9", {"start": v(32.13, 15.25) * mm, "mid": v(32.54, 14.85) * mm, "end": v(33.12, 14.85) * mm});
            skLineSegment(sketch, "E14.25.0", {"start": v(33, 19.05) * mm, "end": v(31.48, 18.07) * mm});
            skArc(sketch, "E14.25.1", {"start": v(31.48, 18.07) * mm, "mid": v(31.15, 17.6) * mm, "end": v(31.22, 17.03) * mm});
            skArc(sketch, "E14.25.2", {"start": v(33, 19.05) * mm, "mid": v(33.72, 20.07) * mm, "end": v(34.3, 21.18) * mm});
            skArc(sketch, "E14.25.3", {"start": v(33.93, 22.4) * mm, "mid": v(33.65, 22.63) * mm, "end": v(33.3, 22.72) * mm});
            skLineSegment(sketch, "E14.25.4", {"start": v(33.93, 22.4) * mm, "end": v(34.1, 22.15) * mm});
            skLineSegment(sketch, "E14.25.5", {"start": v(34.26, 21.9) * mm, "end": v(34.1, 22.15) * mm});
            skArc(sketch, "E14.25.6", {"start": v(34.3, 21.18) * mm, "mid": v(34.36, 21.54) * mm, "end": v(34.26, 21.9) * mm});
            skArc(sketch, "E14.25.7", {"start": v(30.82, 22.4) * mm, "mid": v(32.05, 22.64) * mm, "end": v(33.3, 22.72) * mm});
            skLineSegment(sketch, "E14.25.8", {"start": v(30.82, 22.4) * mm, "end": v(29.3, 21.41) * mm});
            skArc(sketch, "E14.25.9", {"start": v(28.25, 21.6) * mm, "mid": v(28.75, 21.3) * mm, "end": v(29.3, 21.41) * mm});
            skLineSegment(sketch, "E14.26.0", {"start": v(28.31, 25.5) * mm, "end": v(27.04, 24.22) * mm});
            skArc(sketch, "E14.26.1", {"start": v(27.04, 24.22) * mm, "mid": v(26.8, 23.69) * mm, "end": v(27, 23.15) * mm});
            skArc(sketch, "E14.26.2", {"start": v(28.31, 25.5) * mm, "mid": v(28.8, 26.64) * mm, "end": v(29.14, 27.85) * mm});
            skArc(sketch, "E14.26.3", {"start": v(28.54, 28.96) * mm, "mid": v(28.21, 29.13) * mm, "end": v(27.85, 29.14) * mm});
            skLineSegment(sketch, "E14.26.4", {"start": v(28.54, 28.96) * mm, "end": v(28.76, 28.76) * mm});
            skLineSegment(sketch, "E14.26.5", {"start": v(28.96, 28.54) * mm, "end": v(28.76, 28.76) * mm});
            skArc(sketch, "E14.26.6", {"start": v(29.14, 27.85) * mm, "mid": v(29.13, 28.21) * mm, "end": v(28.96, 28.54) * mm});
            skArc(sketch, "E14.26.7", {"start": v(25.5, 28.31) * mm, "mid": v(26.64, 28.8) * mm, "end": v(27.85, 29.14) * mm});
            skLineSegment(sketch, "E14.26.8", {"start": v(25.5, 28.31) * mm, "end": v(24.22, 27.04) * mm});
            skArc(sketch, "E14.26.9", {"start": v(23.15, 27) * mm, "mid": v(23.69, 26.8) * mm, "end": v(24.22, 27.04) * mm});
            skLineSegment(sketch, "E14.27.0", {"start": v(22.4, 30.82) * mm, "end": v(21.41, 29.3) * mm});
            skArc(sketch, "E14.27.1", {"start": v(21.41, 29.3) * mm, "mid": v(21.3, 28.75) * mm, "end": v(21.6, 28.25) * mm});
            skArc(sketch, "E14.27.2", {"start": v(22.4, 30.82) * mm, "mid": v(22.64, 32.05) * mm, "end": v(22.72, 33.3) * mm});
            skArc(sketch, "E14.27.3", {"start": v(21.9, 34.26) * mm, "mid": v(21.54, 34.36) * mm, "end": v(21.18, 34.3) * mm});
            skLineSegment(sketch, "E14.27.4", {"start": v(21.9, 34.26) * mm, "end": v(22.15, 34.1) * mm});
            skLineSegment(sketch, "E14.27.5", {"start": v(22.4, 33.93) * mm, "end": v(22.15, 34.1) * mm});
            skArc(sketch, "E14.27.6", {"start": v(22.72, 33.3) * mm, "mid": v(22.63, 33.65) * mm, "end": v(22.4, 33.93) * mm});
            skArc(sketch, "E14.27.7", {"start": v(19.05, 33) * mm, "mid": v(20.07, 33.72) * mm, "end": v(21.18, 34.3) * mm});
            skLineSegment(sketch, "E14.27.8", {"start": v(19.05, 33) * mm, "end": v(18.07, 31.48) * mm});
            skArc(sketch, "E14.27.9", {"start": v(17.03, 31.22) * mm, "mid": v(17.6, 31.15) * mm, "end": v(18.07, 31.48) * mm});
            skLineSegment(sketch, "E14.28.0", {"start": v(15.5, 34.8) * mm, "end": v(14.85, 33.12) * mm});
            skArc(sketch, "E14.28.1", {"start": v(14.85, 33.12) * mm, "mid": v(14.85, 32.54) * mm, "end": v(15.25, 32.13) * mm});
            skArc(sketch, "E14.28.2", {"start": v(15.5, 34.8) * mm, "mid": v(15.48, 36.06) * mm, "end": v(15.3, 37.3) * mm});
            skArc(sketch, "E14.28.3", {"start": v(14.29, 38.06) * mm, "mid": v(13.92, 38.1) * mm, "end": v(13.58, 37.95) * mm});
            skLineSegment(sketch, "E14.28.4", {"start": v(14.29, 38.06) * mm, "end": v(14.57, 37.97) * mm});
            skLineSegment(sketch, "E14.28.5", {"start": v(14.85, 37.85) * mm, "end": v(14.57, 37.97) * mm});
            skArc(sketch, "E14.28.6", {"start": v(15.3, 37.3) * mm, "mid": v(15.14, 37.62) * mm, "end": v(14.85, 37.85) * mm});
            skArc(sketch, "E14.28.7", {"start": v(11.77, 36.24) * mm, "mid": v(12.62, 37.15) * mm, "end": v(13.58, 37.95) * mm});
            skLineSegment(sketch, "E14.28.8", {"start": v(11.77, 36.24) * mm, "end": v(11.13, 34.55) * mm});
            skArc(sketch, "E14.28.9", {"start": v(10.17, 34.08) * mm, "mid": v(10.74, 34.12) * mm, "end": v(11.13, 34.55) * mm});
            skLineSegment(sketch, "E14.29.0", {"start": v(7.92, 37.27) * mm, "end": v(7.64, 35.48) * mm});
            skArc(sketch, "E14.29.1", {"start": v(7.64, 35.48) * mm, "mid": v(7.76, 34.92) * mm, "end": v(8.23, 34.6) * mm});
            skArc(sketch, "E14.29.2", {"start": v(7.92, 37.27) * mm, "mid": v(7.64, 38.49) * mm, "end": v(7.21, 39.66) * mm});
            skArc(sketch, "E14.29.3", {"start": v(6.06, 40.2) * mm, "mid": v(5.7, 40.15) * mm, "end": v(5.4, 39.95) * mm});
            skLineSegment(sketch, "E14.29.4", {"start": v(6.06, 40.2) * mm, "end": v(6.36, 40.17) * mm});
            skLineSegment(sketch, "E14.29.5", {"start": v(6.66, 40.1) * mm, "end": v(6.36, 40.17) * mm});
            skArc(sketch, "E14.29.6", {"start": v(7.21, 39.66) * mm, "mid": v(6.99, 39.95) * mm, "end": v(6.66, 40.1) * mm});
            skArc(sketch, "E14.29.7", {"start": v(3.98, 37.9) * mm, "mid": v(4.62, 38.96) * mm, "end": v(5.4, 39.95) * mm});
            skLineSegment(sketch, "E14.29.8", {"start": v(3.98, 37.9) * mm, "end": v(3.7, 36.1) * mm});
            skArc(sketch, "E14.29.9", {"start": v(2.86, 35.44) * mm, "mid": v(3.4, 35.61) * mm, "end": v(3.7, 36.1) * mm});
            skArc(sketch, "E15.trimOffspring", {"start": v(2.86, 35.44) * mm, "mid": v(1.86, 35.51) * mm, "end": v(0.86, 35.55) * mm});
            skArc(sketch, "E16.trimOffspring", {"start": v(10.17, 34.08) * mm, "mid": v(9.2, 34.35) * mm, "end": v(8.23, 34.6) * mm});
            skArc(sketch, "E17.trimOffspring", {"start": v(17.03, 31.22) * mm, "mid": v(16.14, 31.68) * mm, "end": v(15.25, 32.13) * mm});
            skArc(sketch, "E18.trimOffspring", {"start": v(28.25, 21.6) * mm, "mid": v(27.64, 22.38) * mm, "end": v(27, 23.15) * mm});
            skArc(sketch, "E19.trimOffspring", {"start": v(23.15, 27) * mm, "mid": v(22.38, 27.64) * mm, "end": v(21.6, 28.25) * mm});
            skArc(sketch, "E20.trimOffspring", {"start": v(32.13, 15.25) * mm, "mid": v(31.68, 16.14) * mm, "end": v(31.22, 17.03) * mm});
            skArc(sketch, "E21.trimOffspring", {"start": v(34.6, 8.23) * mm, "mid": v(34.35, 9.2) * mm, "end": v(34.08, 10.17) * mm});
            skArc(sketch, "E22.trimOffspring", {"start": v(35.55, 0.86) * mm, "mid": v(35.51, 1.86) * mm, "end": v(35.44, 2.86) * mm});
            skArc(sketch, "E23.trimOffspring", {"start": v(34.95, -6.55) * mm, "mid": v(35.12, -5.56) * mm, "end": v(35.26, -4.57) * mm});
            skArc(sketch, "E24.trimOffspring", {"start": v(32.83, -13.67) * mm, "mid": v(33.2, -12.74) * mm, "end": v(33.54, -11.8) * mm});
            skArc(sketch, "E25.trimOffspring", {"start": v(-11.8, 33.54) * mm, "mid": v(-12.74, 33.2) * mm, "end": v(-13.67, 32.83) * mm});
            skArc(sketch, "E26.trimOffspring", {"start": v(-18.52, 30.36) * mm, "mid": v(-19.37, 29.82) * mm, "end": v(-20.2, 29.27) * mm});
            skArc(sketch, "E27.trimOffspring", {"start": v(-24.43, 25.84) * mm, "mid": v(-25.14, 25.14) * mm, "end": v(-25.84, 24.43) * mm});
            skArc(sketch, "E28.trimOffspring", {"start": v(-29.27, 20.2) * mm, "mid": v(-29.82, 19.37) * mm, "end": v(-30.36, 18.52) * mm});
            skArc(sketch, "E29.trimOffspring", {"start": v(-32.83, 13.67) * mm, "mid": v(-33.2, 12.74) * mm, "end": v(-33.54, 11.8) * mm});
            skArc(sketch, "E30.trimOffspring", {"start": v(-34.95, 6.55) * mm, "mid": v(-35.12, 5.56) * mm, "end": v(-35.26, 4.57) * mm});
            skArc(sketch, "E31.trimOffspring", {"start": v(-35.55, -0.86) * mm, "mid": v(-35.51, -1.86) * mm, "end": v(-35.44, -2.86) * mm});
            skArc(sketch, "E32.trimOffspring", {"start": v(-34.6, -8.23) * mm, "mid": v(-34.35, -9.2) * mm, "end": v(-34.08, -10.17) * mm});
            skArc(sketch, "E33.trimOffspring", {"start": v(-32.13, -15.25) * mm, "mid": v(-31.68, -16.14) * mm, "end": v(-31.22, -17.03) * mm});
            skArc(sketch, "E34.trimOffspring", {"start": v(-28.25, -21.6) * mm, "mid": v(-27.64, -22.38) * mm, "end": v(-27, -23.15) * mm});
            skArc(sketch, "E35.trimOffspring", {"start": v(-23.15, -27) * mm, "mid": v(-22.38, -27.64) * mm, "end": v(-21.6, -28.25) * mm});
            skArc(sketch, "E36.trimOffspring", {"start": v(-17.03, -31.22) * mm, "mid": v(-16.14, -31.68) * mm, "end": v(-15.25, -32.13) * mm});
            skArc(sketch, "E37.trimOffspring", {"start": v(-10.17, -34.08) * mm, "mid": v(-9.2, -34.35) * mm, "end": v(-8.23, -34.6) * mm});
            skArc(sketch, "E38.trimOffspring", {"start": v(-2.86, -35.44) * mm, "mid": v(-1.86, -35.51) * mm, "end": v(-0.86, -35.55) * mm});
            skArc(sketch, "E39.trimOffspring", {"start": v(4.57, -35.26) * mm, "mid": v(5.56, -35.12) * mm, "end": v(6.55, -34.95) * mm});
            skArc(sketch, "E40.trimOffspring", {"start": v(11.8, -33.54) * mm, "mid": v(12.74, -33.2) * mm, "end": v(13.67, -32.83) * mm});
            skArc(sketch, "E41.trimOffspring", {"start": v(18.52, -30.36) * mm, "mid": v(19.37, -29.82) * mm, "end": v(20.2, -29.27) * mm});
            skArc(sketch, "E42.trimOffspring", {"start": v(24.43, -25.84) * mm, "mid": v(25.14, -25.14) * mm, "end": v(25.84, -24.43) * mm});
            skArc(sketch, "E43.trimOffspring", {"start": v(29.27, -20.2) * mm, "mid": v(29.82, -19.37) * mm, "end": v(30.36, -18.52) * mm});
            skSolve(sketch);
        }
        {
            var Q0;
            Q0=makeQuery(id+"F0.imprint","IMPRINT",FACE,{"disambiguationData":[TD([[makeQuery(id+"F0.imprint","IMPRINT",EDGE,{"derivedFrom":sQuery(id+"F0.wireOp",EDGE,"E0")}),1.0]])]});
            extrude(context, id + "F1", {"entities" : qUnion([Q0]), "depth" : 114.3 * mm});
        }
        {
            var Q0;
            Q0=makeQuery(id+"F1.opExtrude","CAP_FACE",FACE,{"disambiguationData":[OSD([sQuery(id+"F0.wireOp",EDGE,"E0"),sQuery(id+"F0.wireOp",EDGE,"E1.trimOffspring"),sQuery(id+"F0.wireOp",EDGE,"E2"),sQuery(id+"F0.wireOp",EDGE,"E3"),sQuery(id+"F0.wireOp",EDGE,"E4.MirrorCS"),sQuery(id+"F0.wireOp",EDGE,"E5.MirrorCS"),sQuery(id+"F0.wireOp",EDGE,"E6.MirrorCS"),sQuery(id+"F0.wireOp",EDGE,"E9.filletArc"),sQuery(id+"F0.wireOp",EDGE,"E10.filletArc"),sQuery(id+"F0.wireOp",EDGE,"E11.filletArc"),sQuery(id+"F0.wireOp",EDGE,"E12.filletArc"),sQuery(id+"F0.wireOp",EDGE,"E13"),sQuery(id+"F0.wireOp",EDGE,"E14.1.0"),sQuery(id+"F0.wireOp",EDGE,"E14.1.1"),sQuery(id+"F0.wireOp",EDGE,"E14.1.2"),sQuery(id+"F0.wireOp",EDGE,"E14.1.3"),sQuery(id+"F0.wireOp",EDGE,"E14.1.4"),sQuery(id+"F0.wireOp",EDGE,"E14.1.5"),sQuery(id+"F0.wireOp",EDGE,"E14.1.6"),sQuery(id+"F0.wireOp",EDGE,"E14.1.7"),sQuery(id+"F0.wireOp",EDGE,"E14.1.8"),sQuery(id+"F0.wireOp",EDGE,"E14.1.9"),sQuery(id+"F0.wireOp",EDGE,"E14.2.0"),sQuery(id+"F0.wireOp",EDGE,"E14.2.1"),sQuery(id+"F0.wireOp",EDGE,"E14.2.2"),sQuery(id+"F0.wireOp",EDGE,"E14.2.3"),sQuery(id+"F0.wireOp",EDGE,"E14.2.4"),sQuery(id+"F0.wireOp",EDGE,"E14.2.5"),sQuery(id+"F0.wireOp",EDGE,"E14.2.6"),sQuery(id+"F0.wireOp",EDGE,"E14.2.7"),sQuery(id+"F0.wireOp",EDGE,"E14.2.8"),sQuery(id+"F0.wireOp",EDGE,"E14.2.9"),sQuery(id+"F0.wireOp",EDGE,"E14.3.0"),sQuery(id+"F0.wireOp",EDGE,"E14.3.1"),sQuery(id+"F0.wireOp",EDGE,"E14.3.2"),sQuery(id+"F0.wireOp",EDGE,"E14.3.3"),sQuery(id+"F0.wireOp",EDGE,"E14.3.4"),sQuery(id+"F0.wireOp",EDGE,"E14.3.5"),sQuery(id+"F0.wireOp",EDGE,"E14.3.6"),sQuery(id+"F0.wireOp",EDGE,"E14.3.7"),sQuery(id+"F0.wireOp",EDGE,"E14.3.8"),sQuery(id+"F0.wireOp",EDGE,"E14.3.9"),sQuery(id+"F0.wireOp",EDGE,"E14.4.0"),sQuery(id+"F0.wireOp",EDGE,"E14.4.1"),sQuery(id+"F0.wireOp",EDGE,"E14.4.2"),sQuery(id+"F0.wireOp",EDGE,"E14.4.3"),sQuery(id+"F0.wireOp",EDGE,"E14.4.4"),sQuery(id+"F0.wireOp",EDGE,"E14.4.5"),sQuery(id+"F0.wireOp",EDGE,"E14.4.6"),sQuery(id+"F0.wireOp",EDGE,"E14.4.7"),sQuery(id+"F0.wireOp",EDGE,"E14.4.8"),sQuery(id+"F0.wireOp",EDGE,"E14.4.9"),sQuery(id+"F0.wireOp",EDGE,"E14.5.0"),sQuery(id+"F0.wireOp",EDGE,"E14.5.1"),sQuery(id+"F0.wireOp",EDGE,"E14.5.2"),sQuery(id+"F0.wireOp",EDGE,"E14.5.3"),sQuery(id+"F0.wireOp",EDGE,"E14.5.4"),sQuery(id+"F0.wireOp",EDGE,"E14.5.5"),sQuery(id+"F0.wireOp",EDGE,"E14.5.6"),sQuery(id+"F0.wireOp",EDGE,"E14.5.7"),sQuery(id+"F0.wireOp",EDGE,"E14.5.8"),sQuery(id+"F0.wireOp",EDGE,"E14.5.9"),sQuery(id+"F0.wireOp",EDGE,"E14.6.0"),sQuery(id+"F0.wireOp",EDGE,"E14.6.1"),sQuery(id+"F0.wireOp",EDGE,"E14.6.2"),sQuery(id+"F0.wireOp",EDGE,"E14.6.3"),sQuery(id+"F0.wireOp",EDGE,"E14.6.4"),sQuery(id+"F0.wireOp",EDGE,"E14.6.5"),sQuery(id+"F0.wireOp",EDGE,"E14.6.6"),sQuery(id+"F0.wireOp",EDGE,"E14.6.7"),sQuery(id+"F0.wireOp",EDGE,"E14.6.8"),sQuery(id+"F0.wireOp",EDGE,"E14.6.9"),sQuery(id+"F0.wireOp",EDGE,"E14.7.0"),sQuery(id+"F0.wireOp",EDGE,"E14.7.1"),sQuery(id+"F0.wireOp",EDGE,"E14.7.2"),sQuery(id+"F0.wireOp",EDGE,"E14.7.3"),sQuery(id+"F0.wireOp",EDGE,"E14.7.4"),sQuery(id+"F0.wireOp",EDGE,"E14.7.5"),sQuery(id+"F0.wireOp",EDGE,"E14.7.6"),sQuery(id+"F0.wireOp",EDGE,"E14.7.7"),sQuery(id+"F0.wireOp",EDGE,"E14.7.8"),sQuery(id+"F0.wireOp",EDGE,"E14.7.9"),sQuery(id+"F0.wireOp",EDGE,"E14.8.0"),sQuery(id+"F0.wireOp",EDGE,"E14.8.1"),sQuery(id+"F0.wireOp",EDGE,"E14.8.2"),sQuery(id+"F0.wireOp",EDGE,"E14.8.3"),sQuery(id+"F0.wireOp",EDGE,"E14.8.4"),sQuery(id+"F0.wireOp",EDGE,"E14.8.5"),sQuery(id+"F0.wireOp",EDGE,"E14.8.6"),sQuery(id+"F0.wireOp",EDGE,"E14.8.7"),sQuery(id+"F0.wireOp",EDGE,"E14.8.8"),sQuery(id+"F0.wireOp",EDGE,"E14.8.9"),sQuery(id+"F0.wireOp",EDGE,"E14.9.0"),sQuery(id+"F0.wireOp",EDGE,"E14.9.1"),sQuery(id+"F0.wireOp",EDGE,"E14.9.2"),sQuery(id+"F0.wireOp",EDGE,"E14.9.3"),sQuery(id+"F0.wireOp",EDGE,"E14.9.4"),sQuery(id+"F0.wireOp",EDGE,"E14.9.5"),sQuery(id+"F0.wireOp",EDGE,"E14.9.6"),sQuery(id+"F0.wireOp",EDGE,"E14.9.7"),sQuery(id+"F0.wireOp",EDGE,"E14.9.8"),sQuery(id+"F0.wireOp",EDGE,"E14.9.9"),sQuery(id+"F0.wireOp",EDGE,"E14.10.0"),sQuery(id+"F0.wireOp",EDGE,"E14.10.1"),sQuery(id+"F0.wireOp",EDGE,"E14.10.2"),sQuery(id+"F0.wireOp",EDGE,"E14.10.3"),sQuery(id+"F0.wireOp",EDGE,"E14.10.4"),sQuery(id+"F0.wireOp",EDGE,"E14.10.5"),sQuery(id+"F0.wireOp",EDGE,"E14.10.6"),sQuery(id+"F0.wireOp",EDGE,"E14.10.7"),sQuery(id+"F0.wireOp",EDGE,"E14.10.8"),sQuery(id+"F0.wireOp",EDGE,"E14.10.9"),sQuery(id+"F0.wireOp",EDGE,"E14.11.0"),sQuery(id+"F0.wireOp",EDGE,"E14.11.1"),sQuery(id+"F0.wireOp",EDGE,"E14.11.2"),sQuery(id+"F0.wireOp",EDGE,"E14.11.3"),sQuery(id+"F0.wireOp",EDGE,"E14.11.4"),sQuery(id+"F0.wireOp",EDGE,"E14.11.5"),sQuery(id+"F0.wireOp",EDGE,"E14.11.6"),sQuery(id+"F0.wireOp",EDGE,"E14.11.7"),sQuery(id+"F0.wireOp",EDGE,"E14.11.8"),sQuery(id+"F0.wireOp",EDGE,"E14.11.9"),sQuery(id+"F0.wireOp",EDGE,"E14.12.0"),sQuery(id+"F0.wireOp",EDGE,"E14.12.1"),sQuery(id+"F0.wireOp",EDGE,"E14.12.2"),sQuery(id+"F0.wireOp",EDGE,"E14.12.3"),sQuery(id+"F0.wireOp",EDGE,"E14.12.4"),sQuery(id+"F0.wireOp",EDGE,"E14.12.5"),sQuery(id+"F0.wireOp",EDGE,"E14.12.6"),sQuery(id+"F0.wireOp",EDGE,"E14.12.7"),sQuery(id+"F0.wireOp",EDGE,"E14.12.8"),sQuery(id+"F0.wireOp",EDGE,"E14.12.9"),sQuery(id+"F0.wireOp",EDGE,"E14.13.0"),sQuery(id+"F0.wireOp",EDGE,"E14.13.1"),sQuery(id+"F0.wireOp",EDGE,"E14.13.2"),sQuery(id+"F0.wireOp",EDGE,"E14.13.3"),sQuery(id+"F0.wireOp",EDGE,"E14.13.4"),sQuery(id+"F0.wireOp",EDGE,"E14.13.5"),sQuery(id+"F0.wireOp",EDGE,"E14.13.6"),sQuery(id+"F0.wireOp",EDGE,"E14.13.7"),sQuery(id+"F0.wireOp",EDGE,"E14.13.8"),sQuery(id+"F0.wireOp",EDGE,"E14.13.9"),sQuery(id+"F0.wireOp",EDGE,"E14.14.0"),sQuery(id+"F0.wireOp",EDGE,"E14.14.1"),sQuery(id+"F0.wireOp",EDGE,"E14.14.2"),sQuery(id+"F0.wireOp",EDGE,"E14.14.3"),sQuery(id+"F0.wireOp",EDGE,"E14.14.4"),sQuery(id+"F0.wireOp",EDGE,"E14.14.5"),sQuery(id+"F0.wireOp",EDGE,"E14.14.6"),sQuery(id+"F0.wireOp",EDGE,"E14.14.7"),sQuery(id+"F0.wireOp",EDGE,"E14.14.8"),sQuery(id+"F0.wireOp",EDGE,"E14.14.9"),sQuery(id+"F0.wireOp",EDGE,"E14.15.0"),sQuery(id+"F0.wireOp",EDGE,"E14.15.1"),sQuery(id+"F0.wireOp",EDGE,"E14.15.2"),sQuery(id+"F0.wireOp",EDGE,"E14.15.3"),sQuery(id+"F0.wireOp",EDGE,"E14.15.4"),sQuery(id+"F0.wireOp",EDGE,"E14.15.5"),sQuery(id+"F0.wireOp",EDGE,"E14.15.6"),sQuery(id+"F0.wireOp",EDGE,"E14.15.7"),sQuery(id+"F0.wireOp",EDGE,"E14.15.8"),sQuery(id+"F0.wireOp",EDGE,"E14.15.9"),sQuery(id+"F0.wireOp",EDGE,"E14.16.0"),sQuery(id+"F0.wireOp",EDGE,"E14.16.1"),sQuery(id+"F0.wireOp",EDGE,"E14.16.2"),sQuery(id+"F0.wireOp",EDGE,"E14.16.3"),sQuery(id+"F0.wireOp",EDGE,"E14.16.4"),sQuery(id+"F0.wireOp",EDGE,"E14.16.5"),sQuery(id+"F0.wireOp",EDGE,"E14.16.6"),sQuery(id+"F0.wireOp",EDGE,"E14.16.7"),sQuery(id+"F0.wireOp",EDGE,"E14.16.8"),sQuery(id+"F0.wireOp",EDGE,"E14.16.9"),sQuery(id+"F0.wireOp",EDGE,"E14.17.0"),sQuery(id+"F0.wireOp",EDGE,"E14.17.1"),sQuery(id+"F0.wireOp",EDGE,"E14.17.2"),sQuery(id+"F0.wireOp",EDGE,"E14.17.3"),sQuery(id+"F0.wireOp",EDGE,"E14.17.4"),sQuery(id+"F0.wireOp",EDGE,"E14.17.5"),sQuery(id+"F0.wireOp",EDGE,"E14.17.6"),sQuery(id+"F0.wireOp",EDGE,"E14.17.7"),sQuery(id+"F0.wireOp",EDGE,"E14.17.8"),sQuery(id+"F0.wireOp",EDGE,"E14.17.9"),sQuery(id+"F0.wireOp",EDGE,"E14.18.0"),sQuery(id+"F0.wireOp",EDGE,"E14.18.1"),sQuery(id+"F0.wireOp",EDGE,"E14.18.2"),sQuery(id+"F0.wireOp",EDGE,"E14.18.3"),sQuery(id+"F0.wireOp",EDGE,"E14.18.4"),sQuery(id+"F0.wireOp",EDGE,"E14.18.5"),sQuery(id+"F0.wireOp",EDGE,"E14.18.6"),sQuery(id+"F0.wireOp",EDGE,"E14.18.7"),sQuery(id+"F0.wireOp",EDGE,"E14.18.8"),sQuery(id+"F0.wireOp",EDGE,"E14.18.9"),sQuery(id+"F0.wireOp",EDGE,"E14.19.0"),sQuery(id+"F0.wireOp",EDGE,"E14.19.1"),sQuery(id+"F0.wireOp",EDGE,"E14.19.2"),sQuery(id+"F0.wireOp",EDGE,"E14.19.3"),sQuery(id+"F0.wireOp",EDGE,"E14.19.4"),sQuery(id+"F0.wireOp",EDGE,"E14.19.5"),sQuery(id+"F0.wireOp",EDGE,"E14.19.6"),sQuery(id+"F0.wireOp",EDGE,"E14.19.7"),sQuery(id+"F0.wireOp",EDGE,"E14.19.8"),sQuery(id+"F0.wireOp",EDGE,"E14.19.9"),sQuery(id+"F0.wireOp",EDGE,"E14.20.0"),sQuery(id+"F0.wireOp",EDGE,"E14.20.1"),sQuery(id+"F0.wireOp",EDGE,"E14.20.2"),sQuery(id+"F0.wireOp",EDGE,"E14.20.3"),sQuery(id+"F0.wireOp",EDGE,"E14.20.4"),sQuery(id+"F0.wireOp",EDGE,"E14.20.5"),sQuery(id+"F0.wireOp",EDGE,"E14.20.6"),sQuery(id+"F0.wireOp",EDGE,"E14.20.7"),sQuery(id+"F0.wireOp",EDGE,"E14.20.8"),sQuery(id+"F0.wireOp",EDGE,"E14.20.9"),sQuery(id+"F0.wireOp",EDGE,"E14.21.0"),sQuery(id+"F0.wireOp",EDGE,"E14.21.1"),sQuery(id+"F0.wireOp",EDGE,"E14.21.2"),sQuery(id+"F0.wireOp",EDGE,"E14.21.3"),sQuery(id+"F0.wireOp",EDGE,"E14.21.4"),sQuery(id+"F0.wireOp",EDGE,"E14.21.5"),sQuery(id+"F0.wireOp",EDGE,"E14.21.6"),sQuery(id+"F0.wireOp",EDGE,"E14.21.7"),sQuery(id+"F0.wireOp",EDGE,"E14.21.8"),sQuery(id+"F0.wireOp",EDGE,"E14.21.9"),sQuery(id+"F0.wireOp",EDGE,"E14.22.0"),sQuery(id+"F0.wireOp",EDGE,"E14.22.1"),sQuery(id+"F0.wireOp",EDGE,"E14.22.2"),sQuery(id+"F0.wireOp",EDGE,"E14.22.3"),sQuery(id+"F0.wireOp",EDGE,"E14.22.4"),sQuery(id+"F0.wireOp",EDGE,"E14.22.5"),sQuery(id+"F0.wireOp",EDGE,"E14.22.6"),sQuery(id+"F0.wireOp",EDGE,"E14.22.7"),sQuery(id+"F0.wireOp",EDGE,"E14.22.8"),sQuery(id+"F0.wireOp",EDGE,"E14.22.9"),sQuery(id+"F0.wireOp",EDGE,"E14.23.0"),sQuery(id+"F0.wireOp",EDGE,"E14.23.1"),sQuery(id+"F0.wireOp",EDGE,"E14.23.2"),sQuery(id+"F0.wireOp",EDGE,"E14.23.3"),sQuery(id+"F0.wireOp",EDGE,"E14.23.4"),sQuery(id+"F0.wireOp",EDGE,"E14.23.5"),sQuery(id+"F0.wireOp",EDGE,"E14.23.6"),sQuery(id+"F0.wireOp",EDGE,"E14.23.7"),sQuery(id+"F0.wireOp",EDGE,"E14.23.8"),sQuery(id+"F0.wireOp",EDGE,"E14.23.9"),sQuery(id+"F0.wireOp",EDGE,"E14.24.0"),sQuery(id+"F0.wireOp",EDGE,"E14.24.1"),sQuery(id+"F0.wireOp",EDGE,"E14.24.2"),sQuery(id+"F0.wireOp",EDGE,"E14.24.3"),sQuery(id+"F0.wireOp",EDGE,"E14.24.4"),sQuery(id+"F0.wireOp",EDGE,"E14.24.5"),sQuery(id+"F0.wireOp",EDGE,"E14.24.6"),sQuery(id+"F0.wireOp",EDGE,"E14.24.7"),sQuery(id+"F0.wireOp",EDGE,"E14.24.8"),sQuery(id+"F0.wireOp",EDGE,"E14.24.9"),sQuery(id+"F0.wireOp",EDGE,"E14.25.0"),sQuery(id+"F0.wireOp",EDGE,"E14.25.1"),sQuery(id+"F0.wireOp",EDGE,"E14.25.2"),sQuery(id+"F0.wireOp",EDGE,"E14.25.3"),sQuery(id+"F0.wireOp",EDGE,"E14.25.4"),sQuery(id+"F0.wireOp",EDGE,"E14.25.5"),sQuery(id+"F0.wireOp",EDGE,"E14.25.6"),sQuery(id+"F0.wireOp",EDGE,"E14.25.7"),sQuery(id+"F0.wireOp",EDGE,"E14.25.8"),sQuery(id+"F0.wireOp",EDGE,"E14.25.9"),sQuery(id+"F0.wireOp",EDGE,"E14.26.0"),sQuery(id+"F0.wireOp",EDGE,"E14.26.1"),sQuery(id+"F0.wireOp",EDGE,"E14.26.2"),sQuery(id+"F0.wireOp",EDGE,"E14.26.3"),sQuery(id+"F0.wireOp",EDGE,"E14.26.4"),sQuery(id+"F0.wireOp",EDGE,"E14.26.5"),sQuery(id+"F0.wireOp",EDGE,"E14.26.6"),sQuery(id+"F0.wireOp",EDGE,"E14.26.7"),sQuery(id+"F0.wireOp",EDGE,"E14.26.8"),sQuery(id+"F0.wireOp",EDGE,"E14.26.9"),sQuery(id+"F0.wireOp",EDGE,"E14.27.0"),sQuery(id+"F0.wireOp",EDGE,"E14.27.1"),sQuery(id+"F0.wireOp",EDGE,"E14.27.2"),sQuery(id+"F0.wireOp",EDGE,"E14.27.3"),sQuery(id+"F0.wireOp",EDGE,"E14.27.4"),sQuery(id+"F0.wireOp",EDGE,"E14.27.5"),sQuery(id+"F0.wireOp",EDGE,"E14.27.6"),sQuery(id+"F0.wireOp",EDGE,"E14.27.7"),sQuery(id+"F0.wireOp",EDGE,"E14.27.8"),sQuery(id+"F0.wireOp",EDGE,"E14.27.9"),sQuery(id+"F0.wireOp",EDGE,"E14.28.0"),sQuery(id+"F0.wireOp",EDGE,"E14.28.1"),sQuery(id+"F0.wireOp",EDGE,"E14.28.2"),sQuery(id+"F0.wireOp",EDGE,"E14.28.3"),sQuery(id+"F0.wireOp",EDGE,"E14.28.4"),sQuery(id+"F0.wireOp",EDGE,"E14.28.5"),sQuery(id+"F0.wireOp",EDGE,"E14.28.6"),sQuery(id+"F0.wireOp",EDGE,"E14.28.7"),sQuery(id+"F0.wireOp",EDGE,"E14.28.8"),sQuery(id+"F0.wireOp",EDGE,"E14.28.9"),sQuery(id+"F0.wireOp",EDGE,"E14.29.0"),sQuery(id+"F0.wireOp",EDGE,"E14.29.1"),sQuery(id+"F0.wireOp",EDGE,"E14.29.2"),sQuery(id+"F0.wireOp",EDGE,"E14.29.3"),sQuery(id+"F0.wireOp",EDGE,"E14.29.4"),sQuery(id+"F0.wireOp",EDGE,"E14.29.5"),sQuery(id+"F0.wireOp",EDGE,"E14.29.6"),sQuery(id+"F0.wireOp",EDGE,"E14.29.7"),sQuery(id+"F0.wireOp",EDGE,"E14.29.8"),sQuery(id+"F0.wireOp",EDGE,"E14.29.9"),sQuery(id+"F0.wireOp",EDGE,"E15.trimOffspring"),sQuery(id+"F0.wireOp",EDGE,"E16.trimOffspring"),sQuery(id+"F0.wireOp",EDGE,"E17.trimOffspring"),sQuery(id+"F0.wireOp",EDGE,"E18.trimOffspring"),sQuery(id+"F0.wireOp",EDGE,"E19.trimOffspring"),sQuery(id+"F0.wireOp",EDGE,"E20.trimOffspring"),sQuery(id+"F0.wireOp",EDGE,"E21.trimOffspring"),sQuery(id+"F0.wireOp",EDGE,"E22.trimOffspring"),sQuery(id+"F0.wireOp",EDGE,"E23.trimOffspring"),sQuery(id+"F0.wireOp",EDGE,"E24.trimOffspring"),sQuery(id+"F0.wireOp",EDGE,"E25.trimOffspring"),sQuery(id+"F0.wireOp",EDGE,"E26.trimOffspring"),sQuery(id+"F0.wireOp",EDGE,"E27.trimOffspring"),sQuery(id+"F0.wireOp",EDGE,"E28.trimOffspring"),sQuery(id+"F0.wireOp",EDGE,"E29.trimOffspring"),sQuery(id+"F0.wireOp",EDGE,"E30.trimOffspring"),sQuery(id+"F0.wireOp",EDGE,"E31.trimOffspring"),sQuery(id+"F0.wireOp",EDGE,"E32.trimOffspring"),sQuery(id+"F0.wireOp",EDGE,"E33.trimOffspring"),sQuery(id+"F0.wireOp",EDGE,"E34.trimOffspring"),sQuery(id+"F0.wireOp",EDGE,"E35.trimOffspring"),sQuery(id+"F0.wireOp",EDGE,"E36.trimOffspring"),sQuery(id+"F0.wireOp",EDGE,"E37.trimOffspring"),sQuery(id+"F0.wireOp",EDGE,"E38.trimOffspring"),sQuery(id+"F0.wireOp",EDGE,"E39.trimOffspring"),sQuery(id+"F0.wireOp",EDGE,"E40.trimOffspring"),sQuery(id+"F0.wireOp",EDGE,"E41.trimOffspring"),sQuery(id+"F0.wireOp",EDGE,"E42.trimOffspring"),sQuery(id+"F0.wireOp",EDGE,"E43.trimOffspring")])],"isStart":false});
            var sketch = newSketch(context, id + "F2", { "sketchPlane" : qUnion([Q0])});
            skCircle(sketch, "E44", {"center": v(0, 0) * mm, "radius": 12.7 * mm});
            skSolve(sketch);
        }
        {
            var Q0;
            Q0=makeQuery(id+"F2.imprint","IMPRINT",FACE,{"disambiguationData":[TD([[makeQuery(id+"F2.imprint","IMPRINT",EDGE,{"derivedFrom":sQuery(id+"F2.wireOp",EDGE,"E44")}),1.0]])]});
            extrude(context, id + "F3", {"entities" : qUnion([Q0]), "operationType" : NewBodyOperationType.ADD, "depth" : 12.7 * mm});
        }
    });
